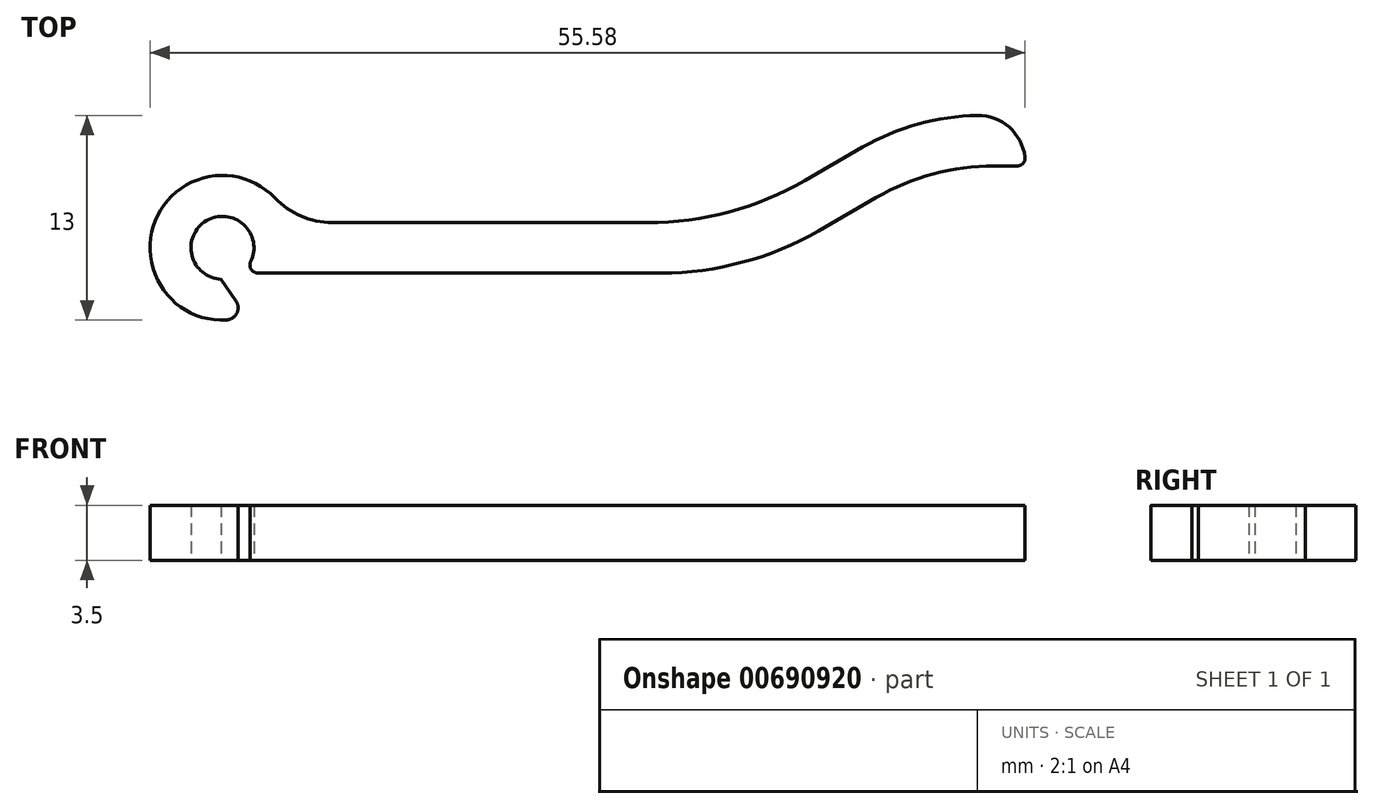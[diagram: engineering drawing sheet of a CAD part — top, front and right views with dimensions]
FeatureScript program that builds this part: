
annotation { "Feature Type Name" : "Feature", "Feature Type Description" : "" }
export const myFeature = defineFeature(function(context is Context, id is Id, definition is map)
    precondition{}
    {
        {
            var Q0;
            Q0=qCreatedBy(makeId("Top.planeOp"),FACE);
            var sketch = newSketch(context, id + "F0", { "sketchPlane" : qUnion([Q0])});
            skArc(sketch, "E0", {"start": v(4.31, 1.6) * mm, "mid": v(-4.17, 1.94) * mm, "end": v(1.55, -4.33) * mm});
            skLineSegment(sketch, "E1", {"start": v(4.31, 1.6) * mm, "end": v(27, 1.6) * mm});
            skLineSegment(sketch, "E2", {"start": v(27.86, -1.6) * mm, "end": v(4.31, -1.6) * mm});
            skLineSegment(sketch, "E3", {"start": v(37, 4.28) * mm, "end": v(40.66, 6.4) * mm});
            skLineSegment(sketch, "E4", {"start": v(41.52, 3.2) * mm, "end": v(37.86, 1.08) * mm});
            skPoint(sketch, "E5.visualSharp", {"position": v(32.36, 1.6) * mm});
            skArc(sketch, "E5.filletArc", {"start": v(27, 1.6) * mm, "mid": v(32.18, 2.28) * mm, "end": v(37, 4.28) * mm});
            skPoint(sketch, "E6.visualSharp", {"position": v(33.22, -1.6) * mm});
            skLineSegment(sketch, "E7", {"start": v(48.16, 8.4) * mm, "end": v(51, 8.4) * mm});
            skLineSegment(sketch, "E8", {"start": v(51, 8.4) * mm, "end": v(51, 5.2) * mm});
            skLineSegment(sketch, "E9", {"start": v(51, 5.2) * mm, "end": v(49.02, 5.2) * mm});
            skPoint(sketch, "E10.visualSharp", {"position": v(44.14, 8.4) * mm});
            skArc(sketch, "E10.filletArc", {"start": v(48.16, 8.4) * mm, "mid": v(44.28, 7.89) * mm, "end": v(40.66, 6.4) * mm});
            skPoint(sketch, "E11.visualSharp", {"position": v(45, 5.2) * mm});
            skArc(sketch, "E11.filletArc", {"start": v(49.02, 5.2) * mm, "mid": v(45.14, 4.69) * mm, "end": v(41.52, 3.2) * mm});
            skArc(sketch, "E12", {"start": v(1.8, -0.88) * mm, "mid": v(-1.02, 1.72) * mm, "end": v(-0.09, -2) * mm});
            skLineSegment(sketch, "E13", {"start": v(4.31, -1.6) * mm, "end": v(2.24, -1.6) * mm});
            skLineSegment(sketch, "E14", {"start": v(-0.09, -2) * mm, "end": v(1.55, -4.33) * mm});
            skPoint(sketch, "E15.visualSharp", {"position": v(1.2, -1.6) * mm});
            skArc(sketch, "E15.filletArc", {"start": v(1.8, -0.88) * mm, "mid": v(1.82, -1.36) * mm, "end": v(2.24, -1.6) * mm});
            skArc(sketch, "E16.filletArc", {"start": v(27.86, -1.6) * mm, "mid": v(33.04, -0.92) * mm, "end": v(37.86, 1.08) * mm});
            skSolve(sketch);
        }
        {
            var Q0;
            Q0=makeQuery(id+"F0.imprint","IMPRINT",FACE,{"disambiguationData":[TD([[makeQuery(id+"F0.imprint","IMPRINT",EDGE,{"derivedFrom":sQuery(id+"F0.wireOp",EDGE,"E0")}),1.0]])]});
            extrude(context, id + "F1", {"entities" : qUnion([Q0]), "depth" : 3.5 * mm, "offsetDistance" : 25 * mm});
        }
        {
            var Q0;
            Q0=makeQuery(id+"F1.opExtrude","SWEPT_EDGE",EDGE,{"disambiguationData":[OSD([sQuery(id+"F0.wireOp",EDGE,"E0"),sQuery(id+"F0.wireOp",EDGE,"E1")])]});
            var Q1;
            Q1=makeQuery(id+"F1.opExtrude","SWEPT_EDGE",EDGE,{"disambiguationData":[OSD([sQuery(id+"F0.wireOp",EDGE,"E2"),sQuery(id+"F0.wireOp",EDGE,"Vh9kxhyG-ojKG-Z7i6-zCEX-T0ziaPJaNEgE")])]});
            fillet(context, id + "F2", {"entities" : qUnion([Q0, Q1]), "radius" : 5 * mm, "tangentPropagation" : true, "allowEdgeOverflow" : false});
        }
        {
            var Q0;
            Q0=makeQuery(id+"F1.opExtrude","SWEPT_EDGE",EDGE,{"disambiguationData":[OSD([sQuery(id+"F0.wireOp",EDGE,"E0"),sQuery(id+"F0.wireOp",EDGE,"DvPdk04V-n24o-38Pd-dKXO-BUPNGXgqHLjk")])]});
            fillet(context, id + "F3", {"entities" : qUnion([Q0]), "radius" : 0.8 * mm, "tangentPropagation" : true, "allowEdgeOverflow" : false});
        }
        {
            var Q0;
            Q0=makeQuery(id+"F1.opExtrude","SWEPT_EDGE",EDGE,{"disambiguationData":[OSD([sQuery(id+"F0.wireOp",EDGE,"E7"),sQuery(id+"F0.wireOp",EDGE,"E8")])]});
            fillet(context, id + "F4", {"entities" : qUnion([Q0]), "radius" : 3 * mm, "tangentPropagation" : true, "allowEdgeOverflow" : false});
        }
        {
            var Q0;
            Q0=makeQuery(id+"F1.opExtrude","SWEPT_EDGE",EDGE,{"disambiguationData":[OSD([sQuery(id+"F0.wireOp",EDGE,"E8"),sQuery(id+"F0.wireOp",EDGE,"E9")])]});
            fillet(context, id + "F5", {"entities" : qUnion([Q0]), "radius" : 0.5 * mm, "tangentPropagation" : true, "allowEdgeOverflow" : false});
        }
    });
